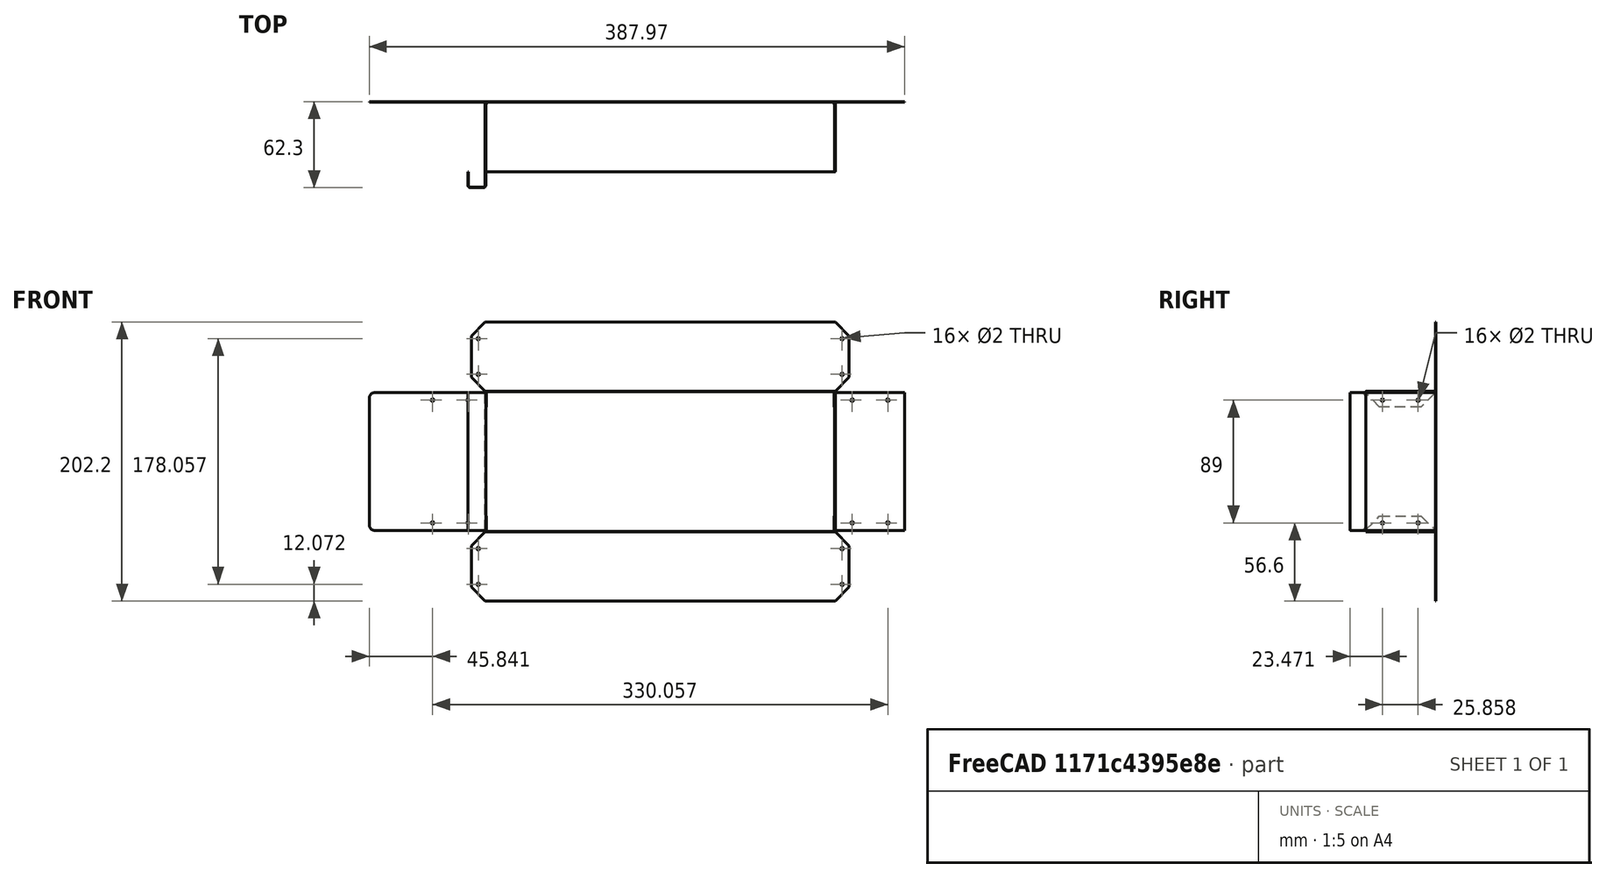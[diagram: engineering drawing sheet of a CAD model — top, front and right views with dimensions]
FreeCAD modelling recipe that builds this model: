
FCSTD DOCUMENT  (FreeCAD 0.21R33771 (Git))
Label: listovoj_metall_korobka2
License: All rights reserved
LicenseURL: https://en.wikipedia.org/wiki/All_rights_reserved
objects: PartDesign::FeaturePython×7, Sketcher::SketchObject×3, PartDesign::Pad×1, PartDesign::Fillet×1, PartDesign::Pocket×1, PartDesign::Body×1, Part::Feature×1
note: 18 computed .brp shape members not serialized (recipe doc carries the construction recipe); baked Part::Feature solids carry a one-line shape summary decoded from their .brp

FEATURE [Sketcher::SketchObject] Sketch
  FullyConstrained = true
  MapMode = 5
  Placement = pos=(0,0,0) rot=(1,0,0;1.5708rad)
  Support = -> [XZ_Plane]
  sketch-geometry (5):
    g0: LineSegment StartX=-125 StartY=-50 StartZ=0 EndX=-125 EndY=50 EndZ=0
    g1: LineSegment StartX=-125 StartY=50 StartZ=0 EndX=125 EndY=50 EndZ=0
    g2: LineSegment StartX=125 StartY=50 StartZ=0 EndX=125 EndY=-50 EndZ=0
    g3: LineSegment StartX=125 StartY=-50 StartZ=0 EndX=-125 EndY=-50 EndZ=0
    g4: GeomPoint X=0 Y=0 Z=0
  constraints (12):
    c: Coincident(g0,g1)
    c: Coincident(g1,g2)
    c: Coincident(g2,g3)
    c: Coincident(g3,g0)
    c: Horizontal(g1)
    c: Horizontal(g3)
    c: Vertical(g0)
    c: Vertical(g2)
    c: Symmetric(g1,g0,g4)
    c: Coincident(g4,g-1)
    c: DistanceY(g2,g2) = 100
    c: DistanceX(g1,g1) = 250
FEATURE [PartDesign::Pad] Pad
  Direction = (0,-1,2e-16)
  Length = 0.4
  Length2 = 10
  Placement = pos=(0,0,0) rot=(1,0,0;1.5708rad)
  Profile = -> Sketch
  ReferenceAxis = -> Sketch [N_Axis]
  Type = 0
FEATURE [PartDesign::FeaturePython] Bend  # WARN: FeaturePython — macro-defined, semantics opaque (R4)
  AutoMiter = true
  BaseFeature = -> Pad
  BendType = 3
  LengthList = [50]
  LengthSpec = 0
  ReliefFactor = 0.7
  UseReliefFactor = false
  angle = 90
  baseObject = -> Pad [Edge10,Edge4]
  bendAList = [90]
  extend1 = 0
  extend2 = 0
  gap1 = 0
  gap2 = 0
  invert = false
  kfactor = 0.5
  length = 50
  maxExtendDist = 5
  minGap = 0.2
  minReliefGap = 1
  miterangle1 = 0
  miterangle2 = 0
  offset = 1
  radius = 0.5
  reliefType = 0
  reliefd = 1
  reliefw = 0.8
  sketchflip = false
  sketchinvert = false
  unfold = false
FEATURE [PartDesign::FeaturePython] Bend001  # WARN: FeaturePython — macro-defined, semantics opaque (R4)
  AutoMiter = true
  BaseFeature = -> Bend
  BendType = 0
  LengthList = [50]
  LengthSpec = 0
  ReliefFactor = 0.7
  UseReliefFactor = false
  angle = 90
  baseObject = -> Bend [Edge32,Edge30]
  bendAList = [90]
  extend1 = 0
  extend2 = 0
  gap1 = 0
  gap2 = 0
  invert = false
  kfactor = 0.5
  length = 50
  maxExtendDist = 5
  minGap = 0.2
  minReliefGap = 1
  miterangle1 = 0
  miterangle2 = 0
  offset = 0
  radius = 0.5
  reliefType = 0
  reliefd = 1
  reliefw = 0.8
  sketchflip = false
  sketchinvert = false
  unfold = false
FEATURE [PartDesign::FeaturePython] Bend002  # WARN: FeaturePython — macro-defined, semantics opaque (R4)
  AutoMiter = false
  BaseFeature = -> Bend001
  BendType = 0
  LengthList = [10]
  LengthSpec = 0
  ReliefFactor = 0.7
  UseReliefFactor = false
  angle = 90
  baseObject = -> Bend001 [Edge70,Edge3]
  bendAList = [90]
  extend1 = 0
  extend2 = 0
  gap1 = 0
  gap2 = 0
  invert = false
  kfactor = 0.5
  length = 10
  maxExtendDist = 5
  minGap = 0.2
  minReliefGap = 1
  miterangle1 = 45
  miterangle2 = 45
  offset = 0
  radius = 1
  reliefType = 0
  reliefd = 1
  reliefw = 0.8
  sketchflip = false
  sketchinvert = false
  unfold = false
FEATURE [PartDesign::FeaturePython] Bend003  # WARN: FeaturePython — macro-defined, semantics opaque (R4)
  AutoMiter = false
  BaseFeature = -> Bend002
  BendType = 0
  LengthList = [10]
  LengthSpec = 0
  ReliefFactor = 0.7
  UseReliefFactor = false
  angle = 90
  baseObject = -> Bend002 [Edge26,Edge84]
  bendAList = [90]
  extend1 = 0
  extend2 = 0
  gap1 = 0
  gap2 = 0
  invert = false
  kfactor = 0.5
  length = 10
  maxExtendDist = 5
  minGap = 0.2
  minReliefGap = 1
  miterangle1 = 45
  miterangle2 = 45
  offset = 0
  radius = 1
  reliefType = 0
  reliefd = 1
  reliefw = 0.8
  sketchflip = false
  sketchinvert = false
  unfold = false
FEATURE [PartDesign::FeaturePython] Extend  # WARN: FeaturePython — macro-defined, semantics opaque (R4)
  BaseFeature = -> Bend003
  Offset = 0.02
  Refine = true
  UseSubtraction = false
  baseObject = -> Bend003 [Edge112]
  gap1 = 0
  gap2 = 0
  length = 10
FEATURE [PartDesign::FeaturePython] Bend004  # WARN: FeaturePython — macro-defined, semantics opaque (R4)
  AutoMiter = true
  BaseFeature = -> Extend
  BendType = 0
  LengthList = [10]
  LengthSpec = 0
  ReliefFactor = 0.7
  UseReliefFactor = false
  angle = 90
  baseObject = -> Extend [Edge63]
  bendAList = [90]
  extend1 = 0
  extend2 = 0
  gap1 = 0
  gap2 = 0
  invert = false
  kfactor = 0.5
  length = 10
  maxExtendDist = 5
  minGap = 0.2
  minReliefGap = 1
  miterangle1 = 0
  miterangle2 = 0
  offset = 0
  radius = 1
  reliefType = 0
  reliefd = 1
  reliefw = 0.8
  sketchflip = false
  sketchinvert = false
  unfold = false
FEATURE [PartDesign::FeaturePython] Bend005  # WARN: FeaturePython — macro-defined, semantics opaque (R4)
  AutoMiter = true
  BaseFeature = -> Bend004
  BendType = 0
  LengthList = [10]
  LengthSpec = 0
  ReliefFactor = 0.7
  UseReliefFactor = false
  angle = 90
  baseObject = -> Bend004 [Edge9]
  bendAList = [90]
  extend1 = 0
  extend2 = 0
  gap1 = 0
  gap2 = 0
  invert = false
  kfactor = 0.5
  length = 10
  maxExtendDist = 5
  minGap = 0.2
  minReliefGap = 1
  miterangle1 = 0
  miterangle2 = 0
  offset = 0
  radius = 1
  reliefType = 0
  reliefd = 1
  reliefw = 0.8
  sketchflip = false
  sketchinvert = false
  unfold = false
FEATURE [PartDesign::Fillet] Fillet
  Base = -> Bend005 [Edge8,Edge2]
  BaseFeature = -> Bend005
  Radius = 4
  SupportTransform = false
  UseAllEdges = false
FEATURE [Sketcher::SketchObject] Sketch001
  ExternalGeometry = -> [Fillet]
  FullyConstrained = true
  MapMode = 5
  Placement = pos=(126.9,1.41e-14,0) rot=(0.57735,0.57735,0.57735;2.0944rad)
  Support = -> [Fillet]
  sketch-geometry (4):
    g0: Circle CenterX=-38.8289 CenterY=44.5 CenterZ=0 NormalX=0 NormalY=0 NormalZ=1 AngleXU=0 Radius=1
    g1: Circle CenterX=-12.9711 CenterY=44.5 CenterZ=0 NormalX=0 NormalY=0 NormalZ=1 AngleXU=0 Radius=1
    g2: Circle CenterX=-38.8289 CenterY=-44.5 CenterZ=0 NormalX=0 NormalY=0 NormalZ=1 AngleXU=0 Radius=1
    g3: Circle CenterX=-12.9711 CenterY=-44.5 CenterZ=0 NormalX=0 NormalY=0 NormalZ=1 AngleXU=0 Radius=1
  constraints (12):
    c: Equal(g2,g3)
    c: Equal(g3,g0)
    c: Equal(g0,g1)
    c: Radius(g0) = 1
    c: Horizontal(g0,g1)
    c: Horizontal(g2,g3)
    c: Vertical(g1,g3)
    c: Vertical(g0,g2)
    c: Distance(g1,g-3) = 5
    c: Distance(g0,g-5) = 5
    c: Distance(g0,g-4) = 5
    c: Distance(g2,g-6) = 5
FEATURE [PartDesign::Pocket] Pocket
  BaseFeature = -> Fillet
  Direction = (-1,0,0)
  Length = 13
  Length2 = 5
  Profile = -> Sketch001
  ReferenceAxis = -> Sketch001 [N_Axis]
  Type = 1
FEATURE [PartDesign::Body] Body
  Group = -> [Sketch,Pad,Bend,Bend001,Bend002,Bend003,Extend,Bend004,Bend005,Fillet,Sketch001,Pocket]
  Origin = -> Origin
  Tip = -> Pocket
FEATURE [Part::Feature] Unfold001
  shape: bbox 388 x 0.4 x 202.2 mm, 48 faces (baked)
FEATURE [Sketcher::SketchObject] Unfold_Sketch001
  FullyConstrained = false
  sketch-geometry (56):
    g0: LineSegment StartX=-91.0996 StartY=-136.885 StartZ=0 EndX=-101.1 EndY=-126.885 EndZ=0
    g1: LineSegment StartX=-61.0996 StartY=-136.885 StartZ=0 EndX=-91.0996 EndY=-136.885 EndZ=0
    g2: LineSegment StartX=-51.0996 StartY=-126.885 StartZ=0 EndX=-61.0996 EndY=-136.885 EndZ=0
    g3: LineSegment StartX=-51.0996 StartY=-126.885 StartZ=0 EndX=-51.0996 EndY=-125 EndZ=0
    g4: LineSegment StartX=-51.0996 StartY=-125 StartZ=0 EndX=-50 EndY=-125 EndZ=0
    g5: LineSegment StartX=-50 StartY=-125 StartZ=0 EndX=-50 EndY=-206.869 EndZ=0
    g6: ArcOfCircle CenterX=-46 CenterY=-206.869 CenterZ=0 NormalX=0 NormalY=0 NormalZ=1 AngleXU=1.5708 Radius=4 StartAngle=1.5708 EndAngle=3.14159
    g7: LineSegment StartX=46 StartY=-210.869 StartZ=0 EndX=-46 EndY=-210.869 EndZ=0
    g8: ArcOfCircle CenterX=46 CenterY=-206.869 CenterZ=0 NormalX=0 NormalY=0 NormalZ=1 AngleXU=1.5708 Radius=4 StartAngle=3.14159 EndAngle=4.71239
    g9: LineSegment StartX=50 StartY=-125 StartZ=0 EndX=50 EndY=-206.869 EndZ=0
    g10: LineSegment StartX=50 StartY=-125 StartZ=0 EndX=51.0996 EndY=-125 EndZ=0
    g11: LineSegment StartX=51.0996 StartY=-125 StartZ=0 EndX=51.0996 EndY=-126.885 EndZ=0
    g12: LineSegment StartX=61.0996 StartY=-136.885 StartZ=0 EndX=51.0996 EndY=-126.885 EndZ=0
    g13: LineSegment StartX=91.0996 StartY=-136.885 StartZ=0 EndX=61.0996 EndY=-136.885 EndZ=0
    g14: LineSegment StartX=101.1 StartY=-126.885 StartZ=0 EndX=91.0996 EndY=-136.885 EndZ=0
    g15: LineSegment StartX=101.1 StartY=-126.885 StartZ=0 EndX=101.1 EndY=126.885 EndZ=0
    g16: LineSegment StartX=91.0996 StartY=136.885 StartZ=0 EndX=101.1 EndY=126.885 EndZ=0
    g17: LineSegment StartX=61.0996 StartY=136.885 StartZ=0 EndX=91.0996 EndY=136.885 EndZ=0
    g18: LineSegment StartX=51.0996 StartY=126.885 StartZ=0 EndX=61.0996 EndY=136.885 EndZ=0
    g19: LineSegment StartX=51.0996 StartY=126.885 StartZ=0 EndX=51.0996 EndY=125 EndZ=0
    g20: LineSegment StartX=51.0996 StartY=125 StartZ=0 EndX=50 EndY=125 EndZ=0
    g21: LineSegment StartX=50 StartY=125 StartZ=0 EndX=50 EndY=177.1 EndZ=0
    g22: LineSegment StartX=-50 StartY=177.1 StartZ=0 EndX=50 EndY=177.1 EndZ=0
    g23: LineSegment StartX=-50 StartY=125 StartZ=0 EndX=-50 EndY=177.1 EndZ=0
    g24: LineSegment StartX=-50 StartY=125 StartZ=0 EndX=-51.0996 EndY=125 EndZ=0
    g25: LineSegment StartX=-51.0996 StartY=125 StartZ=0 EndX=-51.0996 EndY=126.885 EndZ=0
    g26: LineSegment StartX=-61.0996 StartY=136.885 StartZ=0 EndX=-51.0996 EndY=126.885 EndZ=0
    g27: LineSegment StartX=-91.0996 StartY=136.885 StartZ=0 EndX=-61.0996 EndY=136.885 EndZ=0
    g28: LineSegment StartX=-101.1 StartY=126.885 StartZ=0 EndX=-91.0996 EndY=136.885 EndZ=0
    g29: LineSegment StartX=-101.1 StartY=126.885 StartZ=0 EndX=-101.1 EndY=-126.885 EndZ=0
    g30: Circle CenterX=89.0285 CenterY=131.885 CenterZ=0 NormalX=0 NormalY=0 NormalZ=-1 AngleXU=0 Radius=1
    g31: Circle CenterX=-63.1706 CenterY=131.885 CenterZ=0 NormalX=0 NormalY=0 NormalZ=-1 AngleXU=3.14159 Radius=1
    g32: Circle CenterX=-89.0285 CenterY=131.885 CenterZ=0 NormalX=0 NormalY=0 NormalZ=-1 AngleXU=3.14159 Radius=1
    g33: Circle CenterX=-44.5 CenterY=165.028 CenterZ=0 NormalX=0 NormalY=0 NormalZ=-1 AngleXU=-1.5708 Radius=1
    g34: Circle CenterX=44.5 CenterY=165.028 CenterZ=0 NormalX=0 NormalY=0 NormalZ=-1 AngleXU=-1.5708 Radius=1
    g35: Circle CenterX=-44.5 CenterY=139.171 CenterZ=0 NormalX=0 NormalY=0 NormalZ=-1 AngleXU=-1.5708 Radius=1
    g36: Circle CenterX=44.5 CenterY=139.171 CenterZ=0 NormalX=0 NormalY=0 NormalZ=-1 AngleXU=-1.5708 Radius=1
    g37: Circle CenterX=89.0285 CenterY=-131.885 CenterZ=0 NormalX=0 NormalY=0 NormalZ=1 AngleXU=3.14159 Radius=1
    g38: Circle CenterX=63.1706 CenterY=-131.885 CenterZ=0 NormalX=0 NormalY=0 NormalZ=1 AngleXU=3.14159 Radius=1
    g39: Circle CenterX=63.1706 CenterY=131.885 CenterZ=0 NormalX=0 NormalY=0 NormalZ=-1 AngleXU=0 Radius=1
    g40: Circle CenterX=-44.5 CenterY=-139.171 CenterZ=0 NormalX=0 NormalY=0 NormalZ=1 AngleXU=1.5708 Radius=1
    g41: Circle CenterX=-44.5 CenterY=-165.028 CenterZ=0 NormalX=0 NormalY=0 NormalZ=1 AngleXU=1.5708 Radius=1
    g42: Circle CenterX=44.5 CenterY=-139.171 CenterZ=0 NormalX=0 NormalY=0 NormalZ=1 AngleXU=1.5708 Radius=1
    g43: Circle CenterX=44.5 CenterY=-165.028 CenterZ=0 NormalX=0 NormalY=0 NormalZ=1 AngleXU=1.5708 Radius=1
    g44: Circle CenterX=-63.1706 CenterY=-131.885 CenterZ=0 NormalX=0 NormalY=0 NormalZ=1 AngleXU=0 Radius=1
    g45: Circle CenterX=-89.0285 CenterY=-131.885 CenterZ=0 NormalX=0 NormalY=0 NormalZ=1 AngleXU=0 Radius=1
    g46: LineSegment StartX=-101.1 StartY=-125.942 StartZ=0 EndX=-51.0996 EndY=-125.942 EndZ=0
    g47: LineSegment StartX=-51.0996 StartY=125.942 StartZ=0 EndX=-101.1 EndY=125.942 EndZ=0
    g48: LineSegment StartX=-50.5498 StartY=125 StartZ=0 EndX=-50.5498 EndY=-125 EndZ=0
    g49: LineSegment StartX=50 StartY=-199.927 StartZ=0 EndX=-50 EndY=-199.927 EndZ=0
    g50: LineSegment StartX=50 StartY=-188.042 StartZ=0 EndX=-50 EndY=-188.042 EndZ=0
    g51: LineSegment StartX=-50 StartY=-126.55 StartZ=0 EndX=50 EndY=-126.55 EndZ=0
    g52: LineSegment StartX=101.1 StartY=125.942 StartZ=0 EndX=51.0996 EndY=125.942 EndZ=0
    g53: LineSegment StartX=51.0996 StartY=-125.942 StartZ=0 EndX=101.1 EndY=-125.942 EndZ=0
    g54: LineSegment StartX=50.5498 StartY=-125 StartZ=0 EndX=50.5498 EndY=125 EndZ=0
    g55: LineSegment StartX=50 StartY=126.55 StartZ=0 EndX=-50 EndY=126.55 EndZ=0
